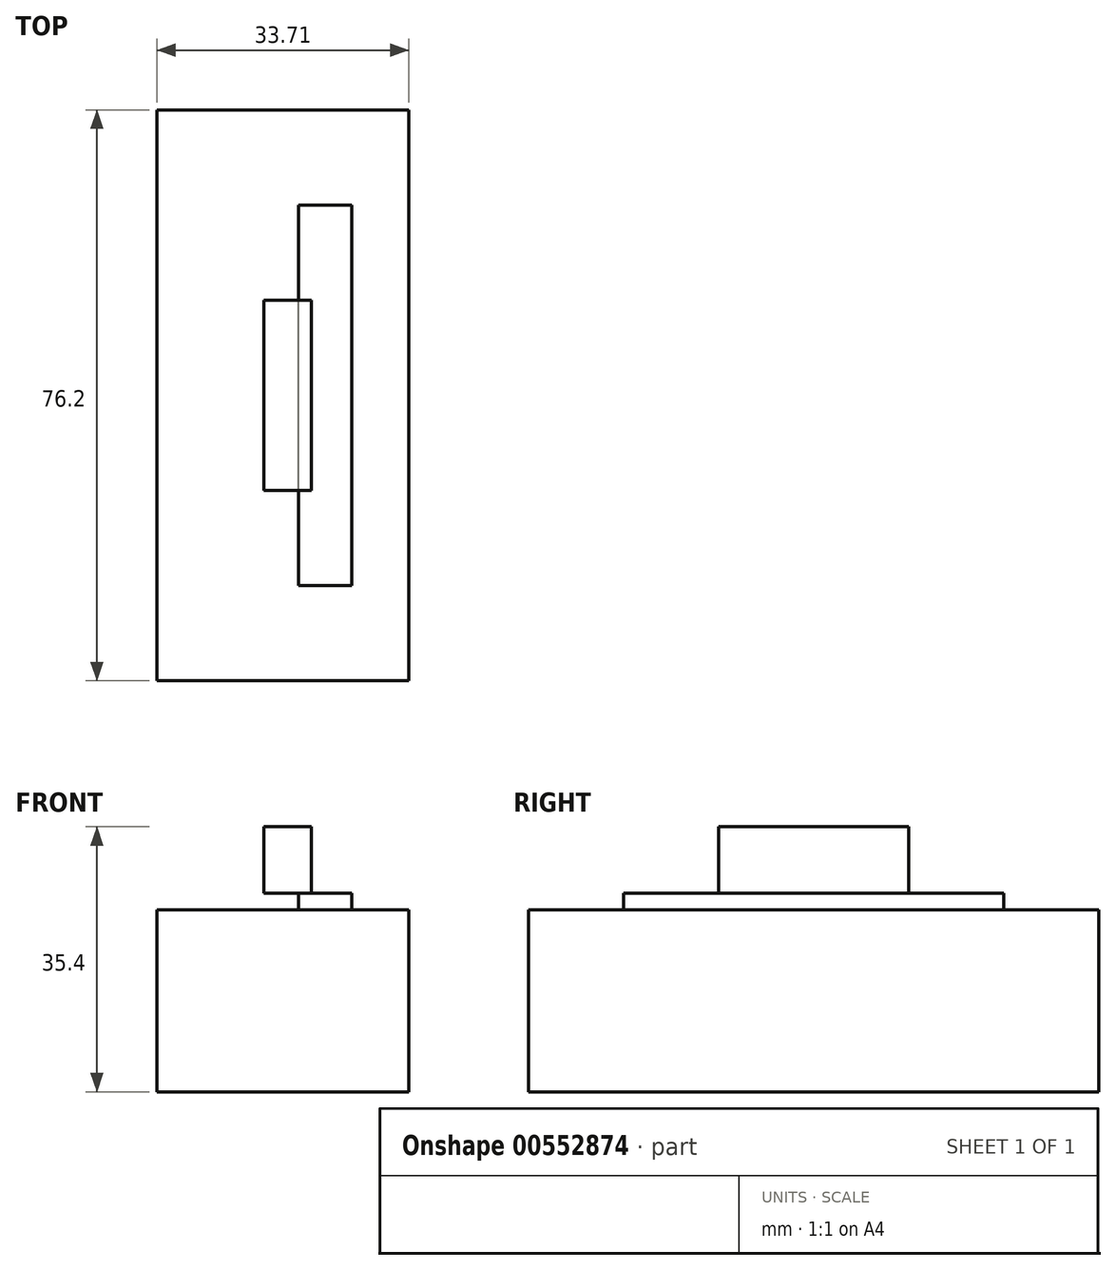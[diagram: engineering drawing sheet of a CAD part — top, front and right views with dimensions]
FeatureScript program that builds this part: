
annotation { "Feature Type Name" : "Feature", "Feature Type Description" : "" }
export const myFeature = defineFeature(function(context is Context, id is Id, definition is map)
    precondition{}
    {
        {
            var Q0;
            Q0=qCreatedBy(makeId("Front.planeOp"),FACE);
            var sketch = newSketch(context, id + "F0", { "sketchPlane" : qUnion([Q0])});
            skLineSegment(sketch, "E0.bottom", {"start": v(-11.43, 18.3) * mm, "end": v(22.28, 18.3) * mm});
            skLineSegment(sketch, "E0.top", {"start": v(-11.43, -5.98) * mm, "end": v(22.28, -5.98) * mm});
            skLineSegment(sketch, "E0.left", {"start": v(-11.43, 18.3) * mm, "end": v(-11.43, -5.98) * mm});
            skLineSegment(sketch, "E0.right", {"start": v(22.28, 18.3) * mm, "end": v(22.28, -5.98) * mm});
            skLineSegment(sketch, "E1.bottom", {"start": v(2.89, 20.53) * mm, "end": v(9.24, 20.53) * mm});
            skLineSegment(sketch, "E1.top", {"start": v(2.89, 29.42) * mm, "end": v(9.24, 29.42) * mm});
            skLineSegment(sketch, "E1.left", {"start": v(2.89, 20.53) * mm, "end": v(2.89, 29.42) * mm});
            skLineSegment(sketch, "E1.right", {"start": v(9.24, 20.53) * mm, "end": v(9.24, 29.42) * mm});
            skLineSegment(sketch, "E2.bottom", {"start": v(7.5, 20.53) * mm, "end": v(14.66, 20.53) * mm});
            skLineSegment(sketch, "E2.top", {"start": v(7.5, 18.3) * mm, "end": v(14.66, 18.3) * mm});
            skLineSegment(sketch, "E2.left", {"start": v(7.5, 20.53) * mm, "end": v(7.5, 18.3) * mm});
            skLineSegment(sketch, "E2.right", {"start": v(14.66, 20.53) * mm, "end": v(14.66, 18.3) * mm});
            skArc(sketch, "E3", {"start": v(-11.43, 18.3) * mm, "mid": v(-7.31, 29.34) * mm, "end": v(3.03, 34.99) * mm});
            skArc(sketch, "E4", {"start": v(3.03, 34.99) * mm, "mid": v(16.46, 31.04) * mm, "end": v(22.28, 18.3) * mm});
            skSolve(sketch);
        }
        {
            var Q0;
            Q0=makeQuery(id+"F0.imprint","IMPRINT",FACE,{"disambiguationData":[TD([[makeQuery(id+"F0.imprint","IMPRINT",EDGE,{"derivedFrom":sQuery(id+"F0.wireOp",EDGE,"E0.top")}),1.0]])]});
            extrude(context, id + "F1", {"entities" : qUnion([Q0]), "endBound" : BoundingType.SYMMETRIC, "depth" : 76.2 * mm, "offsetDistance" : 25.4 * mm});
        }
        {
            var Q0;
            Q0=makeQuery(id+"F0.imprint","IMPRINT",FACE,{"disambiguationData":[TD([[makeQuery(id+"F0.imprint","IMPRINT",EDGE,{"derivedFrom":sQuery(id+"F0.wireOp",EDGE,"E2.bottom")}),-1.0]])]});
            var Q1;
            Q1=makeQuery(id+"F0.imprint","IMPRINT",FACE,{"disambiguationData":[TD([[makeQuery(id+"F0.imprint","IMPRINT",EDGE,{"derivedFrom":sQuery(id+"F0.wireOp",EDGE,"E1.bottom")}),-1.0]])]});
            extrude(context, id + "F2", {"entities" : qUnion([Q0, Q1]), "operationType" : NewBodyOperationType.ADD, "endBound" : BoundingType.SYMMETRIC, "depth" : 50.8 * mm, "offsetDistance" : 25.4 * mm});
        }
        {
            var Q0;
            Q0=makeQuery(id+"F0.imprint","IMPRINT",FACE,{"disambiguationData":[TD([[makeQuery(id+"F0.imprint","IMPRINT",EDGE,{"derivedFrom":sQuery(id+"F0.wireOp",EDGE,"E1.top")}),-1.0]])]});
            extrude(context, id + "F3", {"entities" : qUnion([Q0]), "operationType" : NewBodyOperationType.ADD, "endBound" : BoundingType.SYMMETRIC, "depth" : 25.4 * mm, "offsetDistance" : 25.4 * mm});
        }
    });
